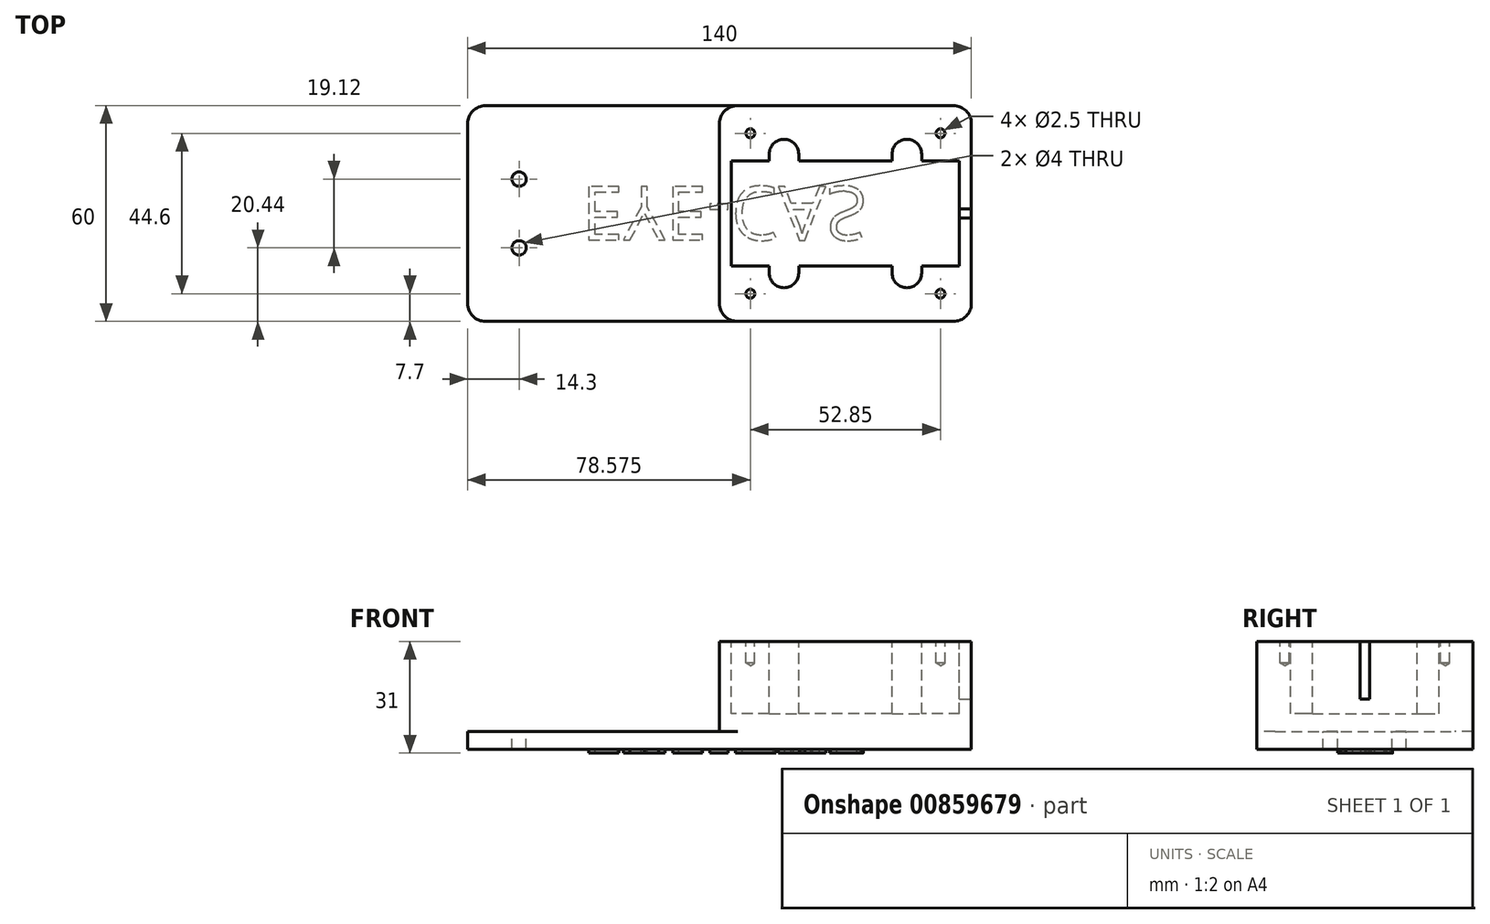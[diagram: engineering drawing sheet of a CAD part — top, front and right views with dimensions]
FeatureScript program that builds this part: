
annotation { "Feature Type Name" : "Feature", "Feature Type Description" : "" }
export const myFeature = defineFeature(function(context is Context, id is Id, definition is map)
    precondition{}
    {
        {
            var Q0;
            Q0=qCreatedBy(makeId("Top.planeOp"),FACE);
            var sketch = newSketch(context, id + "F0", { "sketchPlane" : qUnion([Q0])});
            skLineSegment(sketch, "E0.bottom", {"start": v(70, -30) * mm, "end": v(-70, -30) * mm});
            skLineSegment(sketch, "E0.top", {"start": v(70, 30) * mm, "end": v(-70, 30) * mm});
            skLineSegment(sketch, "E0.left", {"start": v(70, -30) * mm, "end": v(70, 30) * mm});
            skLineSegment(sketch, "E0.right", {"start": v(-70, -30) * mm, "end": v(-70, 30) * mm});
            skPoint(sketch, "E0.middle", {"position": v(0, 0) * mm});
            skSolve(sketch);
        }
        {
            var Q0;
            Q0=makeQuery(id+"F0.imprint","IMPRINT",FACE,{"disambiguationData":[TD([[makeQuery(id+"F0.imprint","IMPRINT",EDGE,{"derivedFrom":sQuery(id+"F0.wireOp",EDGE,"E0.bottom")}),-1.0]])]});
            extrude(context, id + "F1", {"entities" : qUnion([Q0]), "depth" : 5 * mm, "offsetDistance" : 25 * mm});
        }
        {
            var Q0;
            Q0=makeQuery(id+"F1.opExtrude","CAP_FACE",FACE,{"disambiguationData":[OSD([sQuery(id+"F0.wireOp",EDGE,"E0.bottom"),sQuery(id+"F0.wireOp",EDGE,"E0.top"),sQuery(id+"F0.wireOp",EDGE,"E0.left"),sQuery(id+"F0.wireOp",EDGE,"E0.right")])],"isStart":false});
            var sketch = newSketch(context, id + "F2", { "sketchPlane" : qUnion([Q0])});
            skLineSegment(sketch, "E1", {"start": v(70, 30) * mm, "end": v(0, 30) * mm});
            skLineSegment(sketch, "E2", {"start": v(0, 30) * mm, "end": v(0, -30) * mm});
            skLineSegment(sketch, "E3", {"start": v(0, -30) * mm, "end": v(70, -30) * mm});
            skLineSegment(sketch, "E4", {"start": v(70, -30) * mm, "end": v(70, 30) * mm});
            skSolve(sketch);
        }
        {
            var Q0;
            Q0=makeQuery(id+"F2.imprint","IMPRINT",FACE,{"disambiguationData":[TD([[makeQuery(id+"F2.imprint","IMPRINT",EDGE,{"derivedFrom":sQuery(id+"F2.wireOp",EDGE,"E1")}),1.0]])]});
            extrude(context, id + "F3", {"entities" : qUnion([Q0]), "operationType" : NewBodyOperationType.ADD, "depth" : 25 * mm, "offsetDistance" : 25 * mm});
        }
        {
            var Q0;
            Q0=makeQuery(id+"F1.opExtrude","CAP_FACE",FACE,{"disambiguationData":[OSD([sQuery(id+"F0.wireOp",EDGE,"E0.bottom"),sQuery(id+"F0.wireOp",EDGE,"E0.top"),sQuery(id+"F0.wireOp",EDGE,"E0.left"),sQuery(id+"F0.wireOp",EDGE,"E0.right")])],"isStart":false});
            var sketch = newSketch(context, id + "F4", { "sketchPlane" : qUnion([Q0])});
            skLineSegment(sketch, "E5", {"start": v(-55.7, 30) * mm, "end": v(-55.7, -30) * mm});
            skLineSegment(sketch, "E6", {"start": v(-55.7, 0) * mm, "end": v(-70, 0) * mm});
            skCircle(sketch, "E7", {"center": v(-55.7, 9.56) * mm, "radius": 2 * mm});
            skCircle(sketch, "E8", {"center": v(-55.7, -9.56) * mm, "radius": 2 * mm});
            skSolve(sketch);
        }
        {
            var Q0;
            Q0=sQuery(id+"F4.wireOp",VERTEX,"E7.center");
            var Q1;
            Q1=sQuery(id+"F4.wireOp",VERTEX,"E8.center");
            var Q2;
            Q2=makeQuery(id+"F1.opExtrude","SWEPT_BODY",BODY,{"disambiguationData":[OSD([sQuery(id+"F0.wireOp",EDGE,"E0.bottom"),sQuery(id+"F0.wireOp",EDGE,"E0.top"),sQuery(id+"F0.wireOp",EDGE,"E0.left"),sQuery(id+"F0.wireOp",EDGE,"E0.right")])]});
            hole(context, id + "F5", {"style" : HoleStyle.SIMPLE, "endStyle" : HoleEndStyle.THROUGH, "holeDiameter" : 4 * mm, "majorDiameter" : 5 * mm, "isTappedThrough" : true, "tappedDepth" : 12 * mm, "tapClearance" : 3, "locations" : qUnion([Q0, Q1]), "scope" : qUnion([Q2])});
        }
        {
            var Q0;
            Q0=makeQuery(id+"F1.opExtrude","SWEPT_EDGE",EDGE,{"disambiguationData":[OSD([sQuery(id+"F0.wireOp",EDGE,"E0.top"),sQuery(id+"F0.wireOp",EDGE,"E0.right")])]});
            var Q1;
            Q1=makeQuery(id+"F1.opExtrude","SWEPT_EDGE",EDGE,{"disambiguationData":[OSD([sQuery(id+"F0.wireOp",EDGE,"E0.bottom"),sQuery(id+"F0.wireOp",EDGE,"E0.right")])]});
            fillet(context, id + "F6", {"entities" : qUnion([Q0, Q1]), "radius" : 5 * mm, "tangentPropagation" : true, "allowEdgeOverflow" : false});
        }
        {
            var Q0;
            Q0=makeQuery(id+"F3.opExtrude","CAP_FACE",FACE,{"disambiguationData":[OSD([sQuery(id+"F2.wireOp",EDGE,"E1"),sQuery(id+"F2.wireOp",EDGE,"E2"),sQuery(id+"F2.wireOp",EDGE,"E3"),sQuery(id+"F2.wireOp",EDGE,"E4")])],"isStart":false});
            var sketch = newSketch(context, id + "F7", { "sketchPlane" : qUnion([Q0])});
            skLineSegment(sketch, "E9", {"start": v(0, 0) * mm, "end": v(35, 0) * mm});
            skLineSegment(sketch, "E10", {"start": v(35, -30) * mm, "end": v(35, 30) * mm});
            skLineSegment(sketch, "E11.0.0", {"start": v(-142.95, -9.44) * mm, "end": v(-142.95, 19.76) * mm});
            skLineSegment(sketch, "E11.0.1", {"start": v(-142.95, 19.76) * mm, "end": v(-153.45, 19.76) * mm});
            skLineSegment(sketch, "E11.0.2", {"start": v(-153.45, 19.76) * mm, "end": v(-153.45, 21.69) * mm});
            skArc(sketch, "E11.0.3", {"start": v(-153.45, 21.69) * mm, "mid": v(-157.55, 25.79) * mm, "end": v(-161.65, 21.69) * mm});
            skLineSegment(sketch, "E11.0.4", {"start": v(-161.65, 21.69) * mm, "end": v(-161.65, 19.76) * mm});
            skLineSegment(sketch, "E11.0.5", {"start": v(-161.65, 19.76) * mm, "end": v(-187.6, 19.76) * mm});
            skLineSegment(sketch, "E11.0.6", {"start": v(-187.6, 19.76) * mm, "end": v(-187.6, 21.69) * mm});
            skArc(sketch, "E11.0.7", {"start": v(-187.6, 21.69) * mm, "mid": v(-191.7, 25.79) * mm, "end": v(-195.8, 21.69) * mm});
            skLineSegment(sketch, "E11.0.8", {"start": v(-195.8, 21.69) * mm, "end": v(-195.8, 19.76) * mm});
            skLineSegment(sketch, "E11.0.9", {"start": v(-195.8, 19.76) * mm, "end": v(-206.3, 19.76) * mm});
            skLineSegment(sketch, "E11.0.10", {"start": v(-206.3, 19.76) * mm, "end": v(-206.3, -9.44) * mm});
            skLineSegment(sketch, "E11.0.11", {"start": v(-206.3, -9.44) * mm, "end": v(-195.8, -9.44) * mm});
            skLineSegment(sketch, "E11.0.12", {"start": v(-195.8, -9.44) * mm, "end": v(-195.8, -11.37) * mm});
            skArc(sketch, "E11.0.13", {"start": v(-195.8, -11.37) * mm, "mid": v(-191.7, -15.47) * mm, "end": v(-187.6, -11.37) * mm});
            skLineSegment(sketch, "E11.0.14", {"start": v(-187.6, -11.37) * mm, "end": v(-187.6, -9.44) * mm});
            skLineSegment(sketch, "E11.0.15", {"start": v(-187.6, -9.44) * mm, "end": v(-161.65, -9.44) * mm});
            skLineSegment(sketch, "E11.0.16", {"start": v(-161.65, -9.44) * mm, "end": v(-161.65, -11.37) * mm});
            skArc(sketch, "E11.0.17", {"start": v(-161.65, -11.37) * mm, "mid": v(-157.55, -15.47) * mm, "end": v(-153.45, -11.37) * mm});
            skLineSegment(sketch, "E11.0.18", {"start": v(-153.45, -11.37) * mm, "end": v(-153.45, -9.44) * mm});
            skLineSegment(sketch, "E11.0.19", {"start": v(-153.45, -9.44) * mm, "end": v(-142.95, -9.44) * mm});
            skCircle(sketch, "E12.0", {"center": v(-195.3, 5.16) * mm, "radius": 5 * mm});
            skLineSegment(sketch, "E13", {"start": v(-206.3, 3.86) * mm, "end": v(-213.9, 3.86) * mm});
            skLineSegment(sketch, "E14", {"start": v(-213.9, 6.46) * mm, "end": v(-206.3, 6.46) * mm});
            skLineSegment(sketch, "E15.0", {"start": v(-213.9, 3.86) * mm, "end": v(-213.9, 6.46) * mm});
            skLineSegment(sketch, "E16.bottom", {"start": v(66.68, -14.6) * mm, "end": v(56.18, -14.6) * mm});
            skLineSegment(sketch, "E16.top", {"start": v(66.68, 14.6) * mm, "end": v(56.18, 14.6) * mm});
            skLineSegment(sketch, "E16.left", {"start": v(66.68, -14.6) * mm, "end": v(66.68, 14.6) * mm});
            skLineSegment(sketch, "E16.right", {"start": v(3.33, -14.6) * mm, "end": v(3.32, 14.6) * mm});
            skPoint(sketch, "E16.middle", {"position": v(35, 0) * mm});
            skLineSegment(sketch, "E17", {"start": v(56.18, -14.6) * mm, "end": v(56.18, -16.53) * mm});
            skLineSegment(sketch, "E18.MirrorCS", {"start": v(22.02, -14.6) * mm, "end": v(22.02, -16.53) * mm});
            skLineSegment(sketch, "E19.MirrorCS", {"start": v(13.82, -14.6) * mm, "end": v(13.82, -16.53) * mm});
            skLineSegment(sketch, "E20.MirrorCS", {"start": v(70, 0) * mm, "end": v(66.68, 0) * mm});
            skLineSegment(sketch, "E21.MirrorCS", {"start": v(22.02, 14.6) * mm, "end": v(22.02, 16.53) * mm});
            skLineSegment(sketch, "E22.MirrorCS", {"start": v(13.82, 14.6) * mm, "end": v(13.82, 16.53) * mm});
            skLineSegment(sketch, "E23.MirrorCS", {"start": v(47.98, 14.6) * mm, "end": v(47.98, 16.53) * mm});
            skLineSegment(sketch, "E24.MirrorCS", {"start": v(56.18, 14.6) * mm, "end": v(56.18, 16.53) * mm});
            skArc(sketch, "E25", {"start": v(47.98, -16.53) * mm, "mid": v(52.08, -20.63) * mm, "end": v(56.18, -16.53) * mm});
            skArc(sketch, "E26", {"start": v(13.82, -16.53) * mm, "mid": v(17.92, -20.63) * mm, "end": v(22.02, -16.53) * mm});
            skPoint(sketch, "E27.start.orphan", {"position": v(47.98, -14.6) * mm});
            skLineSegment(sketch, "E28", {"start": v(47.98, -14.6) * mm, "end": v(47.98, -16.53) * mm});
            skArc(sketch, "E29.MirrorCS", {"start": v(13.83, 16.53) * mm, "mid": v(17.93, 20.63) * mm, "end": v(22.03, 16.53) * mm});
            skArc(sketch, "E30.MirrorCS", {"start": v(47.98, 16.53) * mm, "mid": v(52.08, 20.63) * mm, "end": v(56.18, 16.53) * mm});
            skLineSegment(sketch, "E31.trimOffspring", {"start": v(13.82, 14.6) * mm, "end": v(3.33, 14.6) * mm});
            skLineSegment(sketch, "E32.trimOffspring", {"start": v(13.82, -14.6) * mm, "end": v(3.33, -14.6) * mm});
            skLineSegment(sketch, "E33.trimOffspring", {"start": v(47.98, -14.6) * mm, "end": v(22.03, -14.6) * mm});
            skLineSegment(sketch, "E34.trimOffspring", {"start": v(47.97, 14.6) * mm, "end": v(22.03, 14.6) * mm});
            skLineSegment(sketch, "E35.trimOffspring", {"start": v(66.68, 0) * mm, "end": v(70, 0) * mm});
            skLineSegment(sketch, "E36.trimOffspring", {"start": v(35, 0) * mm, "end": v(0, 0) * mm});
            skLineSegment(sketch, "E37", {"start": v(35, 0) * mm, "end": v(66.68, 0) * mm});
            skCircle(sketch, "E38", {"center": v(55.68, 0) * mm, "radius": 5.5 * mm});
            skLineSegment(sketch, "E39", {"start": v(66.68, -1.3) * mm, "end": v(74.27, -1.3) * mm});
            skLineSegment(sketch, "E40", {"start": v(74.27, -1.3) * mm, "end": v(74.27, 1.3) * mm});
            skLineSegment(sketch, "E41", {"start": v(74.27, 1.3) * mm, "end": v(66.68, 1.3) * mm});
            skSolve(sketch);
        }
        {
            var Q0;
            {var subQ0=sQuery(id+"F7.wireOp",EDGE,"E21.MirrorCS");Q0=makeQuery(id+"F7.imprint","IMPRINT",FACE,{"disambiguationData":[TD([[makeQuery(id+"F7.imprint","IMPRINT",EDGE,{"derivedFrom":subQ0}),1.0]])]});}
            var Q1;
            {var subQ1=sQuery(id+"F7.wireOp",EDGE,"E18.MirrorCS");Q1=makeQuery(id+"F7.imprint","IMPRINT",FACE,{"disambiguationData":[TD([[makeQuery(id+"F7.imprint","IMPRINT",EDGE,{"derivedFrom":subQ1}),-1.0]])]});}
            var Q2;
            {var subQ11=sQuery(id+"F7.wireOp",EDGE,"E16.bottom");Q2=makeQuery(id+"F7.imprint","IMPRINT",FACE,{"disambiguationData":[TD([[makeQuery(id+"F7.imprint","IMPRINT",EDGE,{"derivedFrom":subQ11}),-1.0]])]});}
            var Q3;
            {var subQ11=sQuery(id+"F7.wireOp",EDGE,"E16.top");Q3=makeQuery(id+"F7.imprint","IMPRINT",FACE,{"disambiguationData":[TD([[makeQuery(id+"F7.imprint","IMPRINT",EDGE,{"derivedFrom":subQ11}),1.0]])]});}
            var Q4;
            {var subQ0=sQuery(id+"F7.wireOp",EDGE,"E38");var subQ1=sQuery(id+"F7.wireOp",EDGE,"E37");var subQ2=makeQuery(id+"F7.imprint","INTERSECT",VERTEX,{"disambiguationData":[OD(0.0)],"derivedFrom":[subQ1,subQ0]});Q4=makeQuery(id+"F7.imprint","IMPRINT",FACE,{"disambiguationData":[TD([[makeQuery(id+"F7.imprint","IMPRINT",EDGE,{"disambiguationData":[TD([[subQ2,-1.0]])],"derivedFrom":subQ1}),-1.0]])]});}
            var Q5;
            {var subQ0=sQuery(id+"F7.wireOp",EDGE,"E38");var subQ1=sQuery(id+"F7.wireOp",EDGE,"E37");var subQ2=makeQuery(id+"F7.imprint","INTERSECT",VERTEX,{"disambiguationData":[OD(0.0)],"derivedFrom":[subQ1,subQ0]});Q5=makeQuery(id+"F7.imprint","IMPRINT",FACE,{"disambiguationData":[TD([[makeQuery(id+"F7.imprint","IMPRINT",EDGE,{"disambiguationData":[TD([[subQ2,-1.0]])],"derivedFrom":subQ1}),1.0]])]});}
            extrude(context, id + "F8", {"entities" : qUnion([Q0, Q1, Q2, Q3, Q4, Q5]), "operationType" : NewBodyOperationType.REMOVE, "oppositeDirection" : true, "depth" : 20 * mm, "offsetDistance" : 25 * mm});
        }
        {
            var Q0;
            Q0=makeQuery(id+"F3.opExtrude","CAP_FACE",FACE,{"disambiguationData":[OSD([sQuery(id+"F2.wireOp",EDGE,"E1"),sQuery(id+"F2.wireOp",EDGE,"E2"),sQuery(id+"F2.wireOp",EDGE,"E3"),sQuery(id+"F2.wireOp",EDGE,"E4")])],"isStart":false});
            var sketch = newSketch(context, id + "F9", { "sketchPlane" : qUnion([Q0])});
            skLineSegment(sketch, "E42", {"start": v(66.68, 14.6) * mm, "end": v(70, 14.6) * mm});
            skLineSegment(sketch, "E43", {"start": v(66.68, -14.6) * mm, "end": v(70, -14.6) * mm});
            skLineSegment(sketch, "E44", {"start": v(70, 0) * mm, "end": v(70, 1.3) * mm});
            skLineSegment(sketch, "E45", {"start": v(70, 1.3) * mm, "end": v(66.68, 1.3) * mm});
            skLineSegment(sketch, "E46", {"start": v(66.68, 1.3) * mm, "end": v(66.68, -1.3) * mm});
            skLineSegment(sketch, "E47", {"start": v(66.68, -1.3) * mm, "end": v(70, -1.3) * mm});
            skLineSegment(sketch, "E48", {"start": v(70, 0) * mm, "end": v(70, -1.3) * mm});
            skLineSegment(sketch, "E49", {"start": v(8.57, 14.6) * mm, "end": v(8.57, 30) * mm});
            skLineSegment(sketch, "E50", {"start": v(8.57, -14.6) * mm, "end": v(8.58, -30) * mm});
            skLineSegment(sketch, "E51", {"start": v(61.43, -14.6) * mm, "end": v(61.43, -30) * mm});
            skLineSegment(sketch, "E52", {"start": v(61.43, 14.6) * mm, "end": v(61.43, 30) * mm});
            skCircle(sketch, "E53", {"center": v(8.57, 22.3) * mm, "radius": 1.25 * mm});
            skCircle(sketch, "E54", {"center": v(61.43, 22.3) * mm, "radius": 1.25 * mm});
            skLineSegment(sketch, "E55", {"start": v(0, 0) * mm, "end": v(66.68, 0) * mm});
            skCircle(sketch, "E56.MirrorC", {"center": v(8.58, -22.3) * mm, "radius": 1.25 * mm});
            skCircle(sketch, "E57.MirrorC", {"center": v(61.43, -22.3) * mm, "radius": 1.25 * mm});
            skSolve(sketch);
        }
        {
            var Q0;
            Q0=sQuery(id+"F9.wireOp",VERTEX,"E53.center");
            var Q1;
            Q1=sQuery(id+"F9.wireOp",VERTEX,"E54.center");
            var Q2;
            Q2=sQuery(id+"F9.wireOp",VERTEX,"E56.MirrorC.center");
            var Q3;
            Q3=sQuery(id+"F9.wireOp",VERTEX,"E57.MirrorC.center");
            var Q4;
            Q4=makeQuery(id+"F1.opExtrude","SWEPT_BODY",BODY,{"disambiguationData":[OSD([sQuery(id+"F0.wireOp",EDGE,"E0.bottom"),sQuery(id+"F0.wireOp",EDGE,"E0.top"),sQuery(id+"F0.wireOp",EDGE,"E0.left"),sQuery(id+"F0.wireOp",EDGE,"E0.right")])]});
            hole(context, id + "F10", {"style" : HoleStyle.SIMPLE, "endStyle" : HoleEndStyle.BLIND, "holeDiameter" : 2.5 * mm, "majorDiameter" : 5 * mm, "holeDepth" : 6 * mm, "isTappedThrough" : true, "tappedDepth" : 12 * mm, "tapClearance" : 3, "locations" : qUnion([Q0, Q1, Q2, Q3]), "scope" : qUnion([Q4])});
        }
        {
            var Q0;
            Q0=makeQuery(id+"F3.opExtrude","CAP_FACE",FACE,{"disambiguationData":[OSD([sQuery(id+"F2.wireOp",EDGE,"E1"),sQuery(id+"F2.wireOp",EDGE,"E2"),sQuery(id+"F2.wireOp",EDGE,"E3"),sQuery(id+"F2.wireOp",EDGE,"E4")])],"isStart":false});
            var sketch = newSketch(context, id + "F11", { "sketchPlane" : qUnion([Q0])});
            skLineSegment(sketch, "E58", {"start": v(66.68, 1.3) * mm, "end": v(70, 1.3) * mm});
            skLineSegment(sketch, "E59", {"start": v(66.68, -1.3) * mm, "end": v(70, -1.3) * mm});
            skLineSegment(sketch, "E60", {"start": v(66.68, 1.3) * mm, "end": v(66.68, -1.3) * mm});
            skLineSegment(sketch, "E61", {"start": v(70, 1.3) * mm, "end": v(70, -1.3) * mm});
            skSolve(sketch);
        }
        {
            var Q0;
            Q0=makeQuery(id+"F11.imprint","IMPRINT",FACE,{"disambiguationData":[TD([[makeQuery(id+"F11.imprint","IMPRINT",EDGE,{"derivedFrom":sQuery(id+"F11.wireOp",EDGE,"E58")}),-1.0]])]});
            extrude(context, id + "F12", {"entities" : qUnion([Q0]), "operationType" : NewBodyOperationType.REMOVE, "oppositeDirection" : true, "depth" : 16 * mm, "offsetDistance" : 25 * mm});
        }
        {
            var Q0;
            Q0=makeQuery(id+"F1.opExtrude","CAP_FACE",FACE,{"disambiguationData":[OSD([sQuery(id+"F0.wireOp",EDGE,"E0.bottom"),sQuery(id+"F0.wireOp",EDGE,"E0.top"),sQuery(id+"F0.wireOp",EDGE,"E0.left"),sQuery(id+"F0.wireOp",EDGE,"E0.right")])],"isStart":true});
            var sketch = newSketch(context, id + "F13", { "sketchPlane" : qUnion([Q0])});
            skText(sketch, "E62", { "text": "EYE-CAS", "fontName": "OpenSans-Regular.ttf"});
            const initialGuessF13  = {"E62": [-0.03833, -0.0075, 1, 0, 0.015]};
            skSetInitialGuess(sketch, initialGuessF13);
            skSolve(sketch);
        }
        {
            var Q0;
            Q0 = qSketchRegion(id + "F13", true);
            extrude(context, id + "F14", {"entities" : qUnion([Q0]), "operationType" : NewBodyOperationType.ADD, "depth" : 1 * mm, "offsetDistance" : 25 * mm});
        }
        {
            var Q0;
            Q0=makeQuery(id+"F3.opExtrude","SWEPT_EDGE",EDGE,{"disambiguationData":[OSD([sQuery(id+"F0.wireOp",EDGE,"E0.bottom"),sQuery(id+"F2.wireOp",EDGE,"E2"),sQuery(id+"F2.wireOp",EDGE,"E3")])]});
            var Q1;
            Q1=makeQuery(id+"F3.boolean.opBoolean","MERGE",EDGE,{"derivedFrom":[makeQuery(id+"F1.opExtrude","SWEPT_EDGE",EDGE,{"disambiguationData":[OSD([sQuery(id+"F0.wireOp",EDGE,"E0.bottom"),sQuery(id+"F0.wireOp",EDGE,"E0.left")])]}),makeQuery(id+"F3.opExtrude","SWEPT_EDGE",EDGE,{"disambiguationData":[OSD([sQuery(id+"F2.wireOp",EDGE,"E3"),sQuery(id+"F2.wireOp",EDGE,"E4")])]})]});
            var Q2;
            Q2=makeQuery(id+"F3.boolean.opBoolean","MERGE",EDGE,{"derivedFrom":[makeQuery(id+"F1.opExtrude","SWEPT_EDGE",EDGE,{"disambiguationData":[OSD([sQuery(id+"F0.wireOp",EDGE,"E0.top"),sQuery(id+"F0.wireOp",EDGE,"E0.left")])]}),makeQuery(id+"F3.opExtrude","SWEPT_EDGE",EDGE,{"disambiguationData":[OSD([sQuery(id+"F2.wireOp",EDGE,"E1"),sQuery(id+"F2.wireOp",EDGE,"E4")])]})]});
            var Q3;
            Q3=makeQuery(id+"F3.opExtrude","SWEPT_EDGE",EDGE,{"disambiguationData":[OSD([sQuery(id+"F0.wireOp",EDGE,"E0.top"),sQuery(id+"F2.wireOp",EDGE,"E1"),sQuery(id+"F2.wireOp",EDGE,"E2")])]});
            fillet(context, id + "F15", {"entities" : qUnion([Q0, Q1, Q2, Q3]), "radius" : 5 * mm, "tangentPropagation" : true, "allowEdgeOverflow" : false});
        }
    });
